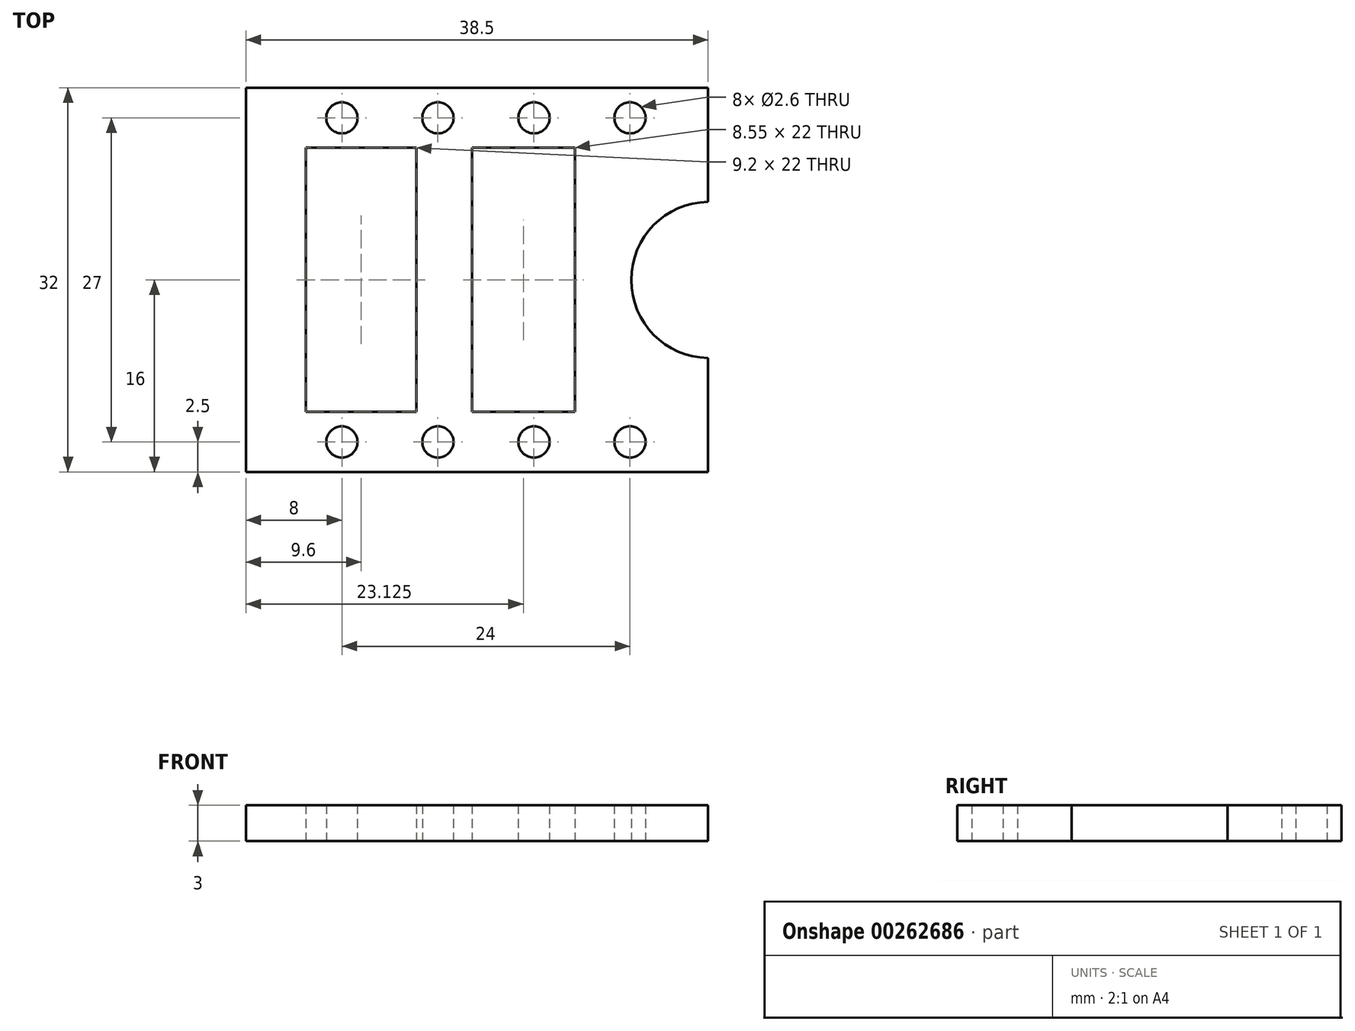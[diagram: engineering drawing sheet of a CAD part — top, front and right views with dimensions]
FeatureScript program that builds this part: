
annotation { "Feature Type Name" : "Feature", "Feature Type Description" : "" }
export const myFeature = defineFeature(function(context is Context, id is Id, definition is map)
    precondition{}
    {
        {
            var Q0;
            Q0=qCreatedBy(makeId("Top.planeOp"),FACE);
            var sketch = newSketch(context, id + "F0", { "sketchPlane" : qUnion([Q0])});
            skLineSegment(sketch, "E0.bottom", {"start": v(19.25, 16) * mm, "end": v(-19.25, 16) * mm});
            skLineSegment(sketch, "E0.top", {"start": v(19.25, -16) * mm, "end": v(-19.25, -16) * mm});
            skLineSegment(sketch, "E0.left", {"start": v(19.25, 16) * mm, "end": v(19.25, -16) * mm});
            skLineSegment(sketch, "E0.right", {"start": v(-19.25, 16) * mm, "end": v(-19.25, -16) * mm});
            skPoint(sketch, "E0.middle", {"position": v(0, 0) * mm});
            skSolve(sketch);
        }
        {
            var Q0;
            Q0=makeQuery(id+"F0.imprint","IMPRINT",FACE,{"disambiguationData":[TD([[makeQuery(id+"F0.imprint","IMPRINT",EDGE,{"derivedFrom":sQuery(id+"F0.wireOp",EDGE,"E0.bottom")}),1.0]])]});
            extrude(context, id + "F1", {"entities" : qUnion([Q0]), "depth" : 3 * mm});
        }
        {
            var Q0;
            Q0=qCreatedBy(makeId("Top.planeOp"),FACE);
            var sketch = newSketch(context, id + "F2", { "sketchPlane" : qUnion([Q0])});
            skLineSegment(sketch, "E1.bottom", {"start": v(-14.25, 11) * mm, "end": v(-5.05, 11) * mm});
            skLineSegment(sketch, "E1.top", {"start": v(-14.25, -11) * mm, "end": v(-5.05, -11) * mm});
            skLineSegment(sketch, "E1.left", {"start": v(-14.25, 11) * mm, "end": v(-14.25, -11) * mm});
            skLineSegment(sketch, "E1.right", {"start": v(-5.05, 11) * mm, "end": v(-5.05, -11) * mm});
            skCircle(sketch, "E2", {"center": v(19.35, 0) * mm, "radius": 6.5 * mm});
            skLineSegment(sketch, "E3.bottom", {"start": v(-0.4, 11) * mm, "end": v(8.15, 11) * mm});
            skLineSegment(sketch, "E3.top", {"start": v(-0.4, -11) * mm, "end": v(8.15, -11) * mm});
            skLineSegment(sketch, "E3.left", {"start": v(-0.4, 11) * mm, "end": v(-0.4, -11) * mm});
            skLineSegment(sketch, "E3.right", {"start": v(8.15, 11) * mm, "end": v(8.15, -11) * mm});
            skLineSegment(sketch, "E4.0", {"start": v(-19.25, 16) * mm, "end": v(-19.25, -16) * mm});
            skCircle(sketch, "E5", {"center": v(-11.25, -13.5) * mm, "radius": 1.3 * mm});
            skLineSegment(sketch, "E6.0", {"start": v(19.25, -16) * mm, "end": v(-19.25, -16) * mm});
            skCircle(sketch, "E7", {"center": v(-3.25, -13.5) * mm, "radius": 1.3 * mm});
            skCircle(sketch, "E8", {"center": v(4.75, -13.5) * mm, "radius": 1.3 * mm});
            skCircle(sketch, "E9", {"center": v(12.75, -13.5) * mm, "radius": 1.3 * mm});
            skCircle(sketch, "E10", {"center": v(-11.25, 13.5) * mm, "radius": 1.3 * mm});
            skCircle(sketch, "E11", {"center": v(-3.25, 13.5) * mm, "radius": 1.3 * mm});
            skCircle(sketch, "E12", {"center": v(4.75, 13.5) * mm, "radius": 1.3 * mm});
            skCircle(sketch, "E13", {"center": v(12.75, 13.5) * mm, "radius": 1.3 * mm});
            skSolve(sketch);
        }
        {
            var Q0;
            Q0 = qSketchRegion(id + "F2", true);
            extrude(context, id + "F3", {"entities" : qUnion([Q0]), "operationType" : NewBodyOperationType.REMOVE, "endBound" : BoundingType.THROUGH_ALL, "depth" : 25 * mm});
        }
    });
